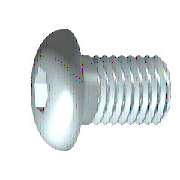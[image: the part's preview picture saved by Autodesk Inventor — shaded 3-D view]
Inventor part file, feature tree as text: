
AUTODESK INVENTOR PART (.ipt)
format: ipt  version: 2015 (Build 190159000, 159)  size: 189,440 bytes
history: native  units: mm (DEFAULTED — no unit token found)
features: sketch x2, extrude x1, plane x1, fillet x1
ambient origin geometry x7: Origin, YZ Plane, XY Plane, X Axis, Y Axis, Z Axis, Center Point
bodies: Solid1 (feature_tree), Body (feature_tree)
feature tree (5):
  extrude  "Slot"  Depth=1.8542mm
  plane  "Work Plane1"
  fillet  "Fillet2"  Radius=1.8542mm
  sketch  "Sketch1"  dims[d1=17.45976mm d2=1.59014mm d3=1.8542mm]
  sketch  "Sketch2"  dims[d4=1.1176mm d5=60.0deg d6=3.5052mm d7=3.5052mm d8=2.287693mm d9=6.6548mm d10=90.0deg d11=10.0mm d12=0.0mm d13=17.45976mm d14=0.0mm d15=0.486918mm d16=0.486918mm d17=1.6002mm d19=0.0mm d26=19.05mm d27=45.0deg d28=0.0mm d29=0.0mm d30=0.1mm]
